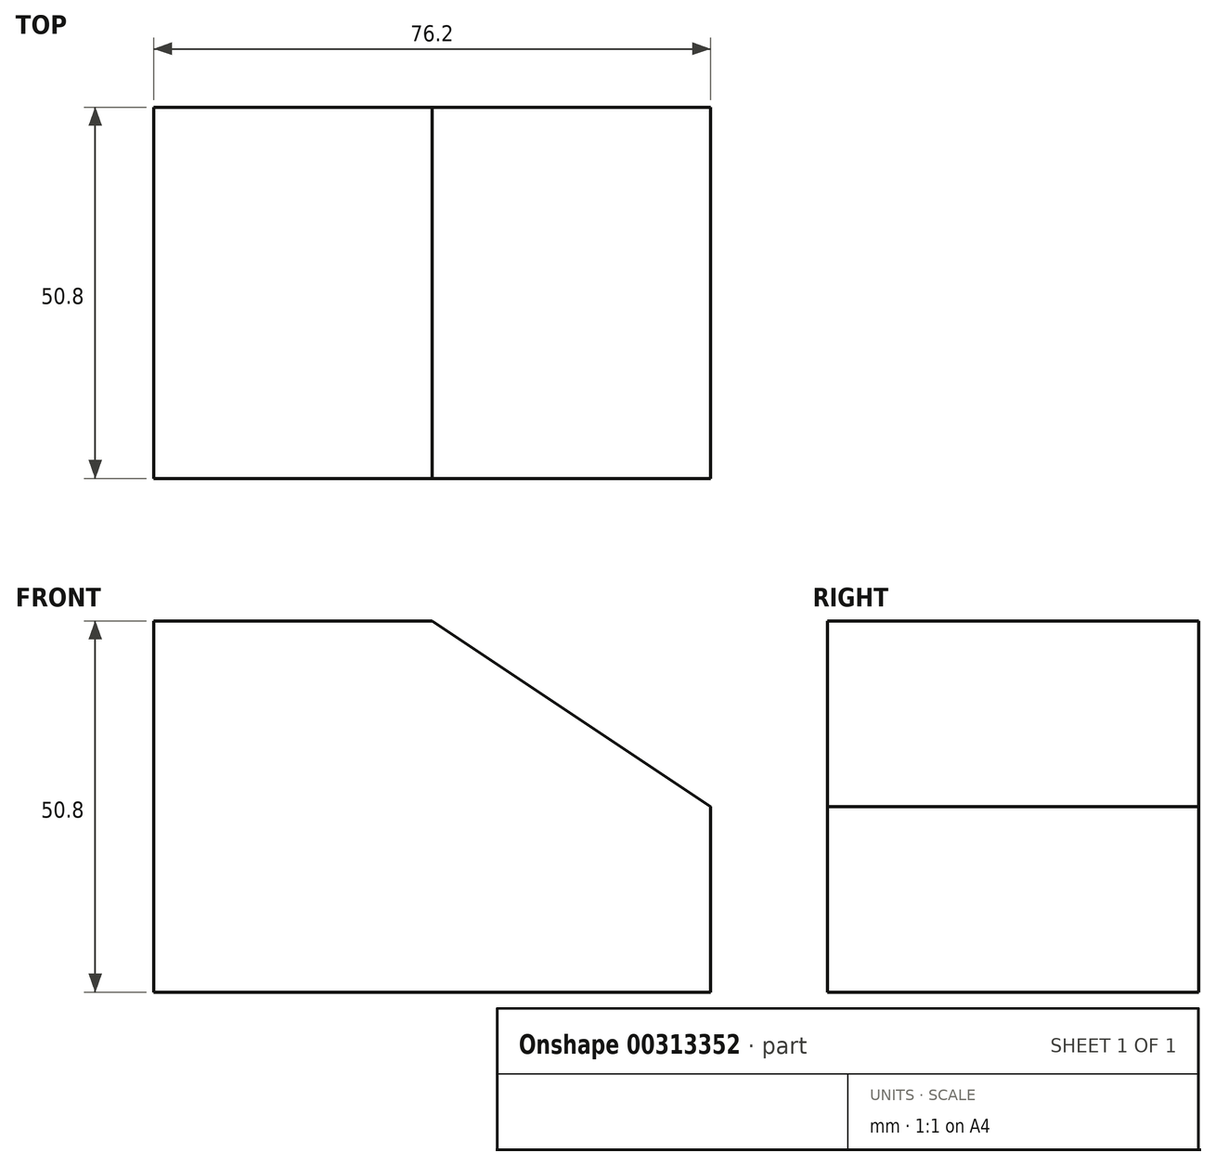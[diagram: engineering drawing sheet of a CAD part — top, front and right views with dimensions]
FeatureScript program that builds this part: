
annotation { "Feature Type Name" : "Feature", "Feature Type Description" : "" }
export const myFeature = defineFeature(function(context is Context, id is Id, definition is map)
    precondition{}
    {
        {
            var Q0;
            Q0=qCreatedBy(makeId("Front.planeOp"),FACE);
            var sketch = newSketch(context, id + "F0", { "sketchPlane" : qUnion([Q0])});
            skLineSegment(sketch, "E0", {"start": v(-30.59, -36.44) * mm, "end": v(45.61, -36.44) * mm});
            skLineSegment(sketch, "E1", {"start": v(-30.59, -36.44) * mm, "end": v(-30.59, 14.36) * mm});
            skLineSegment(sketch, "E2", {"start": v(-30.59, 14.36) * mm, "end": v(7.51, 14.36) * mm});
            skLineSegment(sketch, "E3", {"start": v(45.61, -36.44) * mm, "end": v(45.61, -11.04) * mm});
            skLineSegment(sketch, "E4", {"start": v(45.61, -11.04) * mm, "end": v(7.51, 14.36) * mm});
            skSolve(sketch);
        }
        {
            var Q0;
            Q0=makeQuery(id+"F0.imprint","IMPRINT",FACE,{"disambiguationData":[TD([[makeQuery(id+"F0.imprint","IMPRINT",EDGE,{"derivedFrom":sQuery(id+"F0.wireOp",EDGE,"E0")}),1.0]])]});
            extrude(context, id + "F1", {"entities" : qUnion([Q0]), "depth" : 50.8 * mm});
        }
    });
